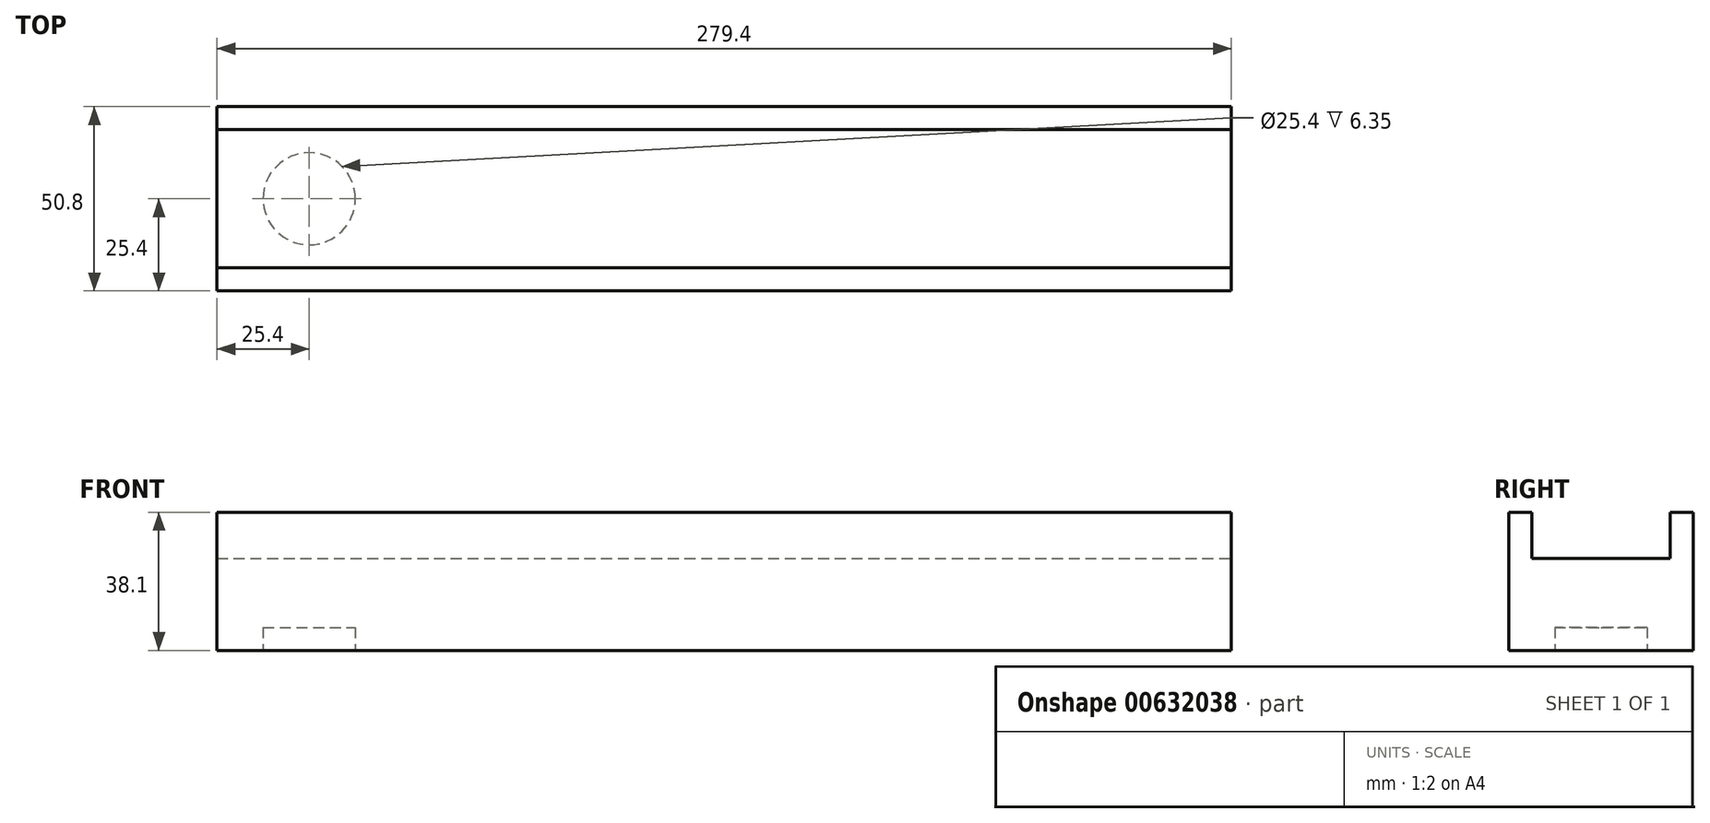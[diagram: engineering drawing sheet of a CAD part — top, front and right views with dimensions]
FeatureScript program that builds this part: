
annotation { "Feature Type Name" : "Feature", "Feature Type Description" : "" }
export const myFeature = defineFeature(function(context is Context, id is Id, definition is map)
    precondition{}
    {
        {
            var Q0;
            Q0=qCreatedBy(makeId("Front.planeOp"),FACE);
            var sketch = newSketch(context, id + "F0", { "sketchPlane" : qUnion([Q0])});
            skLineSegment(sketch, "E0.bottom", {"start": v(0, 0) * mm, "end": v(685.8, 0) * mm});
            skLineSegment(sketch, "E0.top", {"start": v(0, 25.4) * mm, "end": v(685.8, 25.4) * mm});
            skLineSegment(sketch, "E0.left", {"start": v(0, 0) * mm, "end": v(0, 25.4) * mm});
            skLineSegment(sketch, "E0.right", {"start": v(685.8, 0) * mm, "end": v(685.8, 25.4) * mm});
            skSolve(sketch);
        }
        {
            var Q0;
            Q0 = qSketchRegion(id + "F0", true);
            extrude(context, id + "F1", {"entities" : qUnion([Q0]), "depth" : 50.8 * mm, "offsetDistance" : 25.4 * mm});
        }
        {
            var Q0;
            Q0=makeQuery(id+"F1.opExtrude","SWEPT_FACE",FACE,{"disambiguationData":[OSD([sQuery(id+"F0.wireOp",EDGE,"E0.top")])]});
            var sketch = newSketch(context, id + "F2", { "sketchPlane" : qUnion([Q0])});
            skLineSegment(sketch, "E1.bottom", {"start": v(0, -50.8) * mm, "end": v(685.8, -50.8) * mm});
            skLineSegment(sketch, "E1.top", {"start": v(0, -44.45) * mm, "end": v(685.8, -44.45) * mm});
            skLineSegment(sketch, "E1.left", {"start": v(0, -50.8) * mm, "end": v(0, -44.45) * mm});
            skLineSegment(sketch, "E1.right", {"start": v(685.8, -50.8) * mm, "end": v(685.8, -44.45) * mm});
            skLineSegment(sketch, "E2.bottom", {"start": v(0, 0) * mm, "end": v(685.8, 0) * mm});
            skLineSegment(sketch, "E2.top", {"start": v(0, -6.35) * mm, "end": v(685.8, -6.35) * mm});
            skLineSegment(sketch, "E2.left", {"start": v(0, 0) * mm, "end": v(0, -6.35) * mm});
            skLineSegment(sketch, "E2.right", {"start": v(685.8, 0) * mm, "end": v(685.8, -6.35) * mm});
            skSolve(sketch);
        }
        {
            var Q0;
            Q0 = qSketchRegion(id + "F2", true);
            extrude(context, id + "F3", {"entities" : qUnion([Q0]), "operationType" : NewBodyOperationType.ADD, "depth" : 12.7 * mm, "offsetDistance" : 25.4 * mm});
        }
        {
            var Q0;
            Q0=makeQuery(id+"F1.opExtrude","SWEPT_FACE",FACE,{"disambiguationData":[OSD([sQuery(id+"F0.wireOp",EDGE,"E0.bottom")])]});
            var sketch = newSketch(context, id + "F4", { "sketchPlane" : qUnion([Q0])});
            skCircle(sketch, "E3", {"center": v(342.9, 25.4) * mm, "radius": 12.7 * mm});
            skPoint(sketch, "E3.centerSnap0", {"position": v(342.9, 0) * mm});
            skPoint(sketch, "E3.centerSnap1", {"position": v(0, 25.4) * mm});
            skSolve(sketch);
        }
        {
            var Q0;
            Q0 = qSketchRegion(id + "F4", true);
            extrude(context, id + "F5", {"entities" : qUnion([Q0]), "operationType" : NewBodyOperationType.REMOVE, "oppositeDirection" : true, "depth" : 6.35 * mm, "offsetDistance" : 25.4 * mm});
        }
        {
            var Q0;
            Q0=makeQuery(id+"F1.opExtrude","SWEPT_FACE",FACE,{"disambiguationData":[OSD([sQuery(id+"F0.wireOp",EDGE,"E0.bottom")])]});
            var sketch = newSketch(context, id + "F6", { "sketchPlane" : qUnion([Q0])});
            skCircle(sketch, "E4", {"center": v(25.4, 25.4) * mm, "radius": 12.7 * mm});
            skPoint(sketch, "E4.centerSnap0", {"position": v(0, 25.4) * mm});
            skCircle(sketch, "E5", {"center": v(660.4, 25.4) * mm, "radius": 12.7 * mm});
            skPoint(sketch, "E5.centerSnap0", {"position": v(685.8, 25.4) * mm});
            skSolve(sketch);
        }
        {
            var Q0;
            Q0 = qSketchRegion(id + "F6", true);
            extrude(context, id + "F7", {"entities" : qUnion([Q0]), "operationType" : NewBodyOperationType.REMOVE, "oppositeDirection" : true, "depth" : 6.35 * mm, "offsetDistance" : 25.4 * mm});
        }
        {
            var Q0;
            Q0=makeQuery(id+"F3.boolean.opBoolean","MERGE",FACE,{"derivedFrom":[makeQuery(id+"F1.opExtrude","CAP_FACE",FACE,{"disambiguationData":[OSD([sQuery(id+"F0.wireOp",EDGE,"E0.bottom"),sQuery(id+"F0.wireOp",EDGE,"E0.top"),sQuery(id+"F0.wireOp",EDGE,"E0.left"),sQuery(id+"F0.wireOp",EDGE,"E0.right")])],"isStart":false}),makeQuery(id+"F3.opExtrude","SWEPT_FACE",FACE,{"disambiguationData":[OSD([sQuery(id+"F2.wireOp",EDGE,"E1.bottom")])]})]});
            var sketch = newSketch(context, id + "F8", { "sketchPlane" : qUnion([Q0])});
            skLineSegment(sketch, "E6.bottom", {"start": v(279.4, 0) * mm, "end": v(685.8, 0) * mm});
            skLineSegment(sketch, "E6.top", {"start": v(279.4, 38.1) * mm, "end": v(685.8, 38.1) * mm});
            skLineSegment(sketch, "E6.left", {"start": v(279.4, 0) * mm, "end": v(279.4, 38.1) * mm});
            skLineSegment(sketch, "E6.right", {"start": v(685.8, 0) * mm, "end": v(685.8, 38.1) * mm});
            skSolve(sketch);
        }
        {
            var Q0;
            Q0 = qSketchRegion(id + "F8", true);
            extrude(context, id + "F9", {"entities" : qUnion([Q0]), "operationType" : NewBodyOperationType.REMOVE, "oppositeDirection" : true, "depth" : 50.8 * mm, "offsetDistance" : 25.4 * mm});
        }
    });
